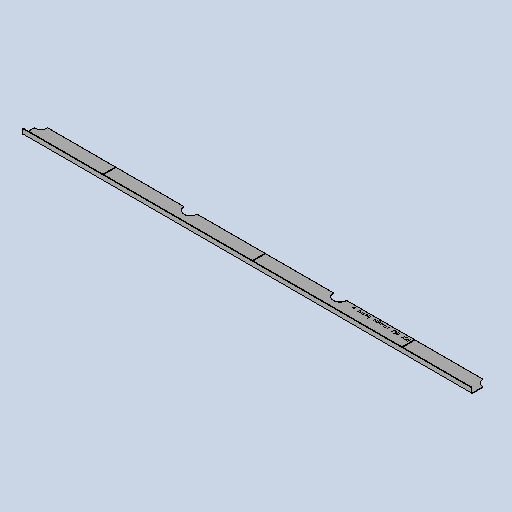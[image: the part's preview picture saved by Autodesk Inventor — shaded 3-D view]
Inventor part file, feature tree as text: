
AUTODESK INVENTOR PART (.ipt)
format: ipt  version: 2025 (Build 290162010, 162A)  size: 315,392 bytes
history: native  units: mm
features: sketch x6, other x5, sheet_metal_op x4, extrude x3, mirror x2, pattern_linear x1, projected_geometry x1
ambient origin geometry x8: Origin, YZ Plane, XZ Plane, XY Plane, X Axis, Y Axis, Z Axis, Center Point
bodies: Solid1 (feature_tree)
feature tree (22):
  sheet_metal_op  "Face1"
  sheet_metal_op  "Flange1"
  extrude  "Extrusion1"  Depth=62.0mm
  pattern_linear  "Rectangular Pattern1"  Count1=2 Spacing1=90.0deg
  extrude  "Extrusion2"  Depth=8.0mm
  mirror  "Mirror1"
  extrude  "Extrusion3"  Depth=2.0mm
  mirror  "Mirror2"
  other  "Mark2"
  other  "A-Side Definition"
  sketch  "Sketch1"  dims[d0=1500.0mm d1=62.0mm]
  other  "Plate1"
  sketch  "Sketch2"  dims[d2=2.0mm]
  other  "Plate2"
  sheet_metal_op  "Bend1"
  sheet_metal_op  "Corner1"
  sketch  "Sketch5"  dims[d3=2.0mm]
  sketch  "Sketch6"  dims[d4=1.0mm]
  sketch  "Sketch7"  dims[d5=4.0mm]
  projected_geometry  "Projected Loop3"
  sketch  "Sketch8"  dims[d6=2.75mm d7=20.0mm d8=90.0deg d9=2.75mm d10=8.0mm d11=2.0mm d12=2.75mm d15=0.0mm d16=0.0mm d18=2.0mm d21=30.0mm d23=500.0mm d24=45.0mm d25=30.0mm d26=0.0mm d27=2.0mm d28=20.0mm d29=100.0mm d30=10.0mm d31=0.0mm d32=0.0mm d33=200.0mm d34=12.0mm d37=5.0mm d38=5.0mm]
  other  "Definition1"
